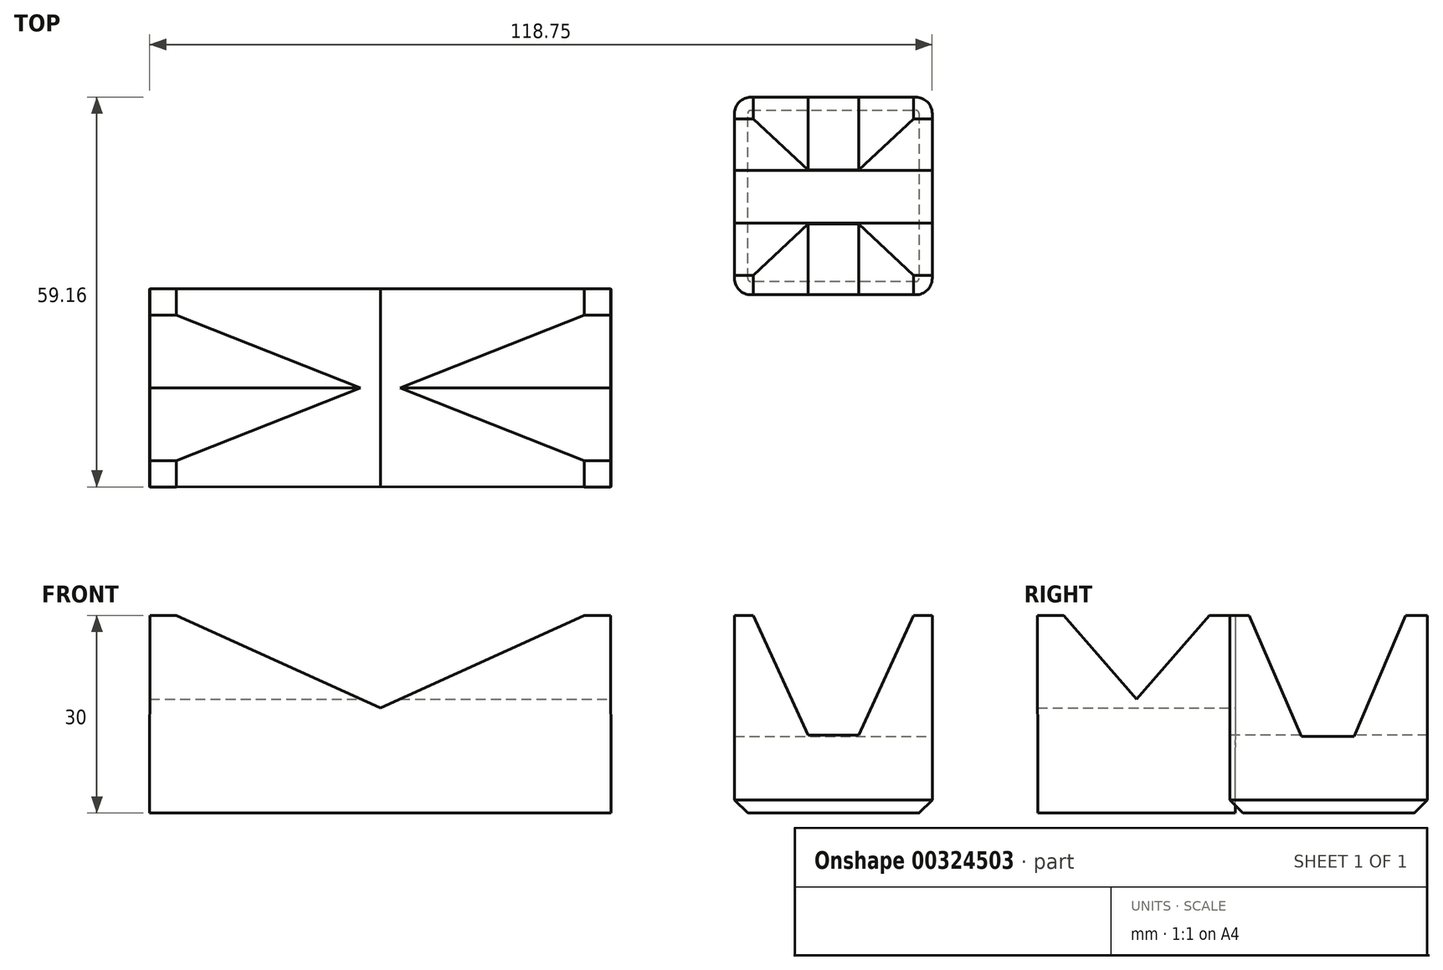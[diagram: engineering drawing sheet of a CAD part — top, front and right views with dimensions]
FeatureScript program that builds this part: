
annotation { "Feature Type Name" : "Feature", "Feature Type Description" : "" }
export const myFeature = defineFeature(function(context is Context, id is Id, definition is map)
    precondition{}
    {
        {
            var Q0;
            Q0=qCreatedBy(makeId("Top.planeOp"),FACE);
            var sketch = newSketch(context, id + "F0", { "sketchPlane" : qUnion([Q0])});
            skLineSegment(sketch, "E0.bottom", {"start": v(-35, 15) * mm, "end": v(35, 15) * mm});
            skLineSegment(sketch, "E0.top", {"start": v(-35, -15) * mm, "end": v(35, -15) * mm});
            skLineSegment(sketch, "E0.left", {"start": v(-35, 15) * mm, "end": v(-35, -15) * mm});
            skLineSegment(sketch, "E0.right", {"start": v(35, 15) * mm, "end": v(35, -15) * mm});
            skPoint(sketch, "E0.middle", {"position": v(0, 0) * mm});
            skSolve(sketch);
        }
        {
            var Q0;
            Q0=qCreatedBy(makeId("Top.planeOp"),FACE);
            cPlane(context, id + "F1", {"entities" : qUnion([Q0]), "cplaneType" : CPlaneType.OFFSET, "offset" : 30 * mm, "width" : 150 * mm, "height" : 150 * mm});
        }
        {
            var Q0;
            Q0=qCreatedBy(id+"F1.planeOp",FACE);
            var sketch = newSketch(context, id + "F2", { "sketchPlane" : qUnion([Q0])});
            skLineSegment(sketch, "E1", {"start": v(-34.94, 15.03) * mm, "end": v(-30.94, 15.03) * mm});
            skLineSegment(sketch, "E2", {"start": v(-30.94, 15.03) * mm, "end": v(-30.94, 11.03) * mm});
            skLineSegment(sketch, "E3", {"start": v(-30.94, 11.03) * mm, "end": v(-34.94, 11.03) * mm});
            skLineSegment(sketch, "E4", {"start": v(-34.94, 11.03) * mm, "end": v(-34.94, 15.03) * mm});
            skLineSegment(sketch, "E5.MirrorCS", {"start": v(-30.94, -15.03) * mm, "end": v(-30.94, -11.03) * mm});
            skLineSegment(sketch, "E6.MirrorCS", {"start": v(-34.94, -15.03) * mm, "end": v(-30.94, -15.03) * mm});
            skLineSegment(sketch, "E7.MirrorCS", {"start": v(-34.94, -11.03) * mm, "end": v(-34.94, -15.03) * mm});
            skLineSegment(sketch, "E8.MirrorCS", {"start": v(-30.94, -11.03) * mm, "end": v(-34.94, -11.03) * mm});
            skLineSegment(sketch, "E9.MirrorCS", {"start": v(30.94, 15.03) * mm, "end": v(30.94, 11.03) * mm});
            skLineSegment(sketch, "E10.MirrorCS", {"start": v(34.94, 15.03) * mm, "end": v(30.94, 15.03) * mm});
            skLineSegment(sketch, "E11.MirrorCS", {"start": v(34.94, 11.03) * mm, "end": v(34.94, 15.03) * mm});
            skLineSegment(sketch, "E12.MirrorCS", {"start": v(30.94, 11.03) * mm, "end": v(34.94, 11.03) * mm});
            skLineSegment(sketch, "E13.MirrorCS", {"start": v(30.94, -11.03) * mm, "end": v(34.94, -11.03) * mm});
            skLineSegment(sketch, "E14.MirrorCS", {"start": v(30.94, -15.03) * mm, "end": v(30.94, -11.03) * mm});
            skLineSegment(sketch, "E15.MirrorCS", {"start": v(34.94, -15.03) * mm, "end": v(30.94, -15.03) * mm});
            skLineSegment(sketch, "E16.MirrorCS", {"start": v(34.94, -11.03) * mm, "end": v(34.94, -15.03) * mm});
            skSolve(sketch);
        }
        {
            var Q0;
            Q0=makeQuery(id+"F0.imprint","IMPRINT",FACE,{"disambiguationData":[TD([[makeQuery(id+"F0.imprint","IMPRINT",EDGE,{"derivedFrom":sQuery(id+"F0.wireOp",EDGE,"E0.bottom")}),-1.0]])]});
            var Q1;
            Q1=makeQuery(id+"F2.imprint","IMPRINT",FACE,{"disambiguationData":[TD([[makeQuery(id+"F2.imprint","IMPRINT",EDGE,{"derivedFrom":sQuery(id+"F2.wireOp",EDGE,"E1")}),-1.0]])]});
            loft(context, id + "F3", {"sheetProfilesArray" : [{ "sheetProfileEntities" : qUnion([Q0]) }, { "sheetProfileEntities" : qUnion([Q1]) }]});
        }
        {
            var Q1;
            Q1 = qSketchRegion(id + "F0", true);
            var Q2;
            Q2=makeQuery(id+"F2.imprint","IMPRINT",FACE,{"disambiguationData":[TD([[makeQuery(id+"F2.imprint","IMPRINT",EDGE,{"derivedFrom":sQuery(id+"F2.wireOp",EDGE,"E5.MirrorCS")}),1.0]])]});
            loft(context, id + "F4", {"operationType" : NewBodyOperationType.ADD, "sheetProfilesArray" : [{ "sheetProfileEntities" : qUnion([Q1]) }, { "sheetProfileEntities" : qUnion([Q2]) }]});
        }
        {
            var Q1;
            Q1 = qSketchRegion(id + "F0", true);
            var Q2;
            Q2=makeQuery(id+"F2.imprint","IMPRINT",FACE,{"disambiguationData":[TD([[makeQuery(id+"F2.imprint","IMPRINT",EDGE,{"derivedFrom":sQuery(id+"F2.wireOp",EDGE,"E9.MirrorCS")}),1.0]])]});
            loft(context, id + "F5", {"operationType" : NewBodyOperationType.ADD, "sheetProfilesArray" : [{ "sheetProfileEntities" : qUnion([Q1]) }, { "sheetProfileEntities" : qUnion([Q2]) }]});
        }
        {
            var Q1;
            Q1 = qSketchRegion(id + "F0", true);
            var Q2;
            Q2=makeQuery(id+"F2.imprint","IMPRINT",FACE,{"disambiguationData":[TD([[makeQuery(id+"F2.imprint","IMPRINT",EDGE,{"derivedFrom":sQuery(id+"F2.wireOp",EDGE,"E13.MirrorCS")}),-1.0]])]});
            loft(context, id + "F6", {"operationType" : NewBodyOperationType.ADD, "sheetProfilesArray" : [{ "sheetProfileEntities" : qUnion([Q1]) }, { "sheetProfileEntities" : qUnion([Q2]) }]});
        }
        {
            var Q0;
            Q0=qCreatedBy(makeId("Top.planeOp"),FACE);
            var sketch = newSketch(context, id + "F7", { "sketchPlane" : qUnion([Q0])});
            skLineSegment(sketch, "E17", {"start": v(83.75, 44.13) * mm, "end": v(53.75, 44.13) * mm});
            skLineSegment(sketch, "E18", {"start": v(53.75, 44.13) * mm, "end": v(53.75, 14.13) * mm});
            skLineSegment(sketch, "E19", {"start": v(53.75, 14.13) * mm, "end": v(83.75, 14.13) * mm});
            skLineSegment(sketch, "E20", {"start": v(83.75, 14.13) * mm, "end": v(83.75, 44.13) * mm});
            skSolve(sketch);
        }
        {
            var Q0;
            Q0=makeQuery(id+"F7.imprint","IMPRINT",FACE,{"disambiguationData":[TD([[makeQuery(id+"F7.imprint","IMPRINT",EDGE,{"derivedFrom":sQuery(id+"F7.wireOp",EDGE,"E17")}),1.0]])]});
            extrude(context, id + "F8", {"entities" : qUnion([Q0]), "depth" : 30 * mm});
        }
        {
            var Q0;
            Q0=makeQuery(id+"F8.opExtrude","SWEPT_FACE",FACE,{"disambiguationData":[OSD([sQuery(id+"F7.wireOp",EDGE,"E19")])]});
            var sketch = newSketch(context, id + "F9", { "sketchPlane" : qUnion([Q0])});
            skLineSegment(sketch, "E21", {"start": v(56.6, 30) * mm, "end": v(64.93, 11.82) * mm});
            skLineSegment(sketch, "E22", {"start": v(64.93, 11.82) * mm, "end": v(68.75, 11.82) * mm});
            skLineSegment(sketch, "E23.MirrorCS", {"start": v(80.91, 30) * mm, "end": v(72.58, 11.82) * mm});
            skLineSegment(sketch, "E24.MirrorCS", {"start": v(72.58, 11.82) * mm, "end": v(68.75, 11.82) * mm});
            skSolve(sketch);
        }
        {
            var Q0;
            {var subQ1=sQuery(id+"F9.wireOp",EDGE,"E21");Q0=makeQuery(id+"F9.imprint","IMPRINT",FACE,{"disambiguationData":[TD([[makeQuery(id+"F9.imprint","IMPRINT",EDGE,{"derivedFrom":subQ1}),1.0]])]});}
            extrude(context, id + "F10", {"entities" : qUnion([Q0]), "operationType" : NewBodyOperationType.REMOVE, "oppositeDirection" : true, "depth" : 30 * mm});
        }
        {
            var Q0;
            Q0=makeQuery(id+"F8.opExtrude","SWEPT_FACE",FACE,{"disambiguationData":[OSD([sQuery(id+"F7.wireOp",EDGE,"E20")])]});
            var sketch = newSketch(context, id + "F11", { "sketchPlane" : qUnion([Q0])});
            skLineSegment(sketch, "E25", {"start": v(17.09, 30) * mm, "end": v(24.99, 11.63) * mm});
            skLineSegment(sketch, "E26", {"start": v(24.99, 11.63) * mm, "end": v(32.99, 11.63) * mm});
            skLineSegment(sketch, "E27", {"start": v(32.99, 11.63) * mm, "end": v(40.82, 30) * mm});
            skSolve(sketch);
        }
        {
            var Q0;
            {var subQ0=sQuery(id+"F11.wireOp",EDGE,"E25");Q0=makeQuery(id+"F11.imprint","IMPRINT",FACE,{"disambiguationData":[TD([[makeQuery(id+"F11.imprint","IMPRINT",EDGE,{"derivedFrom":subQ0}),1.0]])]});}
            extrude(context, id + "F12", {"entities" : qUnion([Q0]), "operationType" : NewBodyOperationType.REMOVE, "oppositeDirection" : true, "depth" : 30 * mm});
        }
        {
            var Q0;
            Q0=makeQuery(id+"F8.opExtrude","SWEPT_EDGE",EDGE,{"disambiguationData":[OSD([sQuery(id+"F7.wireOp",EDGE,"E19"),sQuery(id+"F7.wireOp",EDGE,"E20")])]});
            var Q1;
            Q1=makeQuery(id+"F8.opExtrude","SWEPT_EDGE",EDGE,{"disambiguationData":[OSD([sQuery(id+"F7.wireOp",EDGE,"E18"),sQuery(id+"F7.wireOp",EDGE,"E19")])]});
            var Q2;
            Q2=makeQuery(id+"F8.opExtrude","SWEPT_EDGE",EDGE,{"disambiguationData":[OSD([sQuery(id+"F7.wireOp",EDGE,"E17"),sQuery(id+"F7.wireOp",EDGE,"E20")])]});
            var Q3;
            Q3=makeQuery(id+"F8.opExtrude","SWEPT_EDGE",EDGE,{"disambiguationData":[OSD([sQuery(id+"F7.wireOp",EDGE,"E17"),sQuery(id+"F7.wireOp",EDGE,"E18")])]});
            fillet(context, id + "F13", {"entities" : qUnion([Q0, Q1, Q2, Q3]), "radius" : 2.5 * mm, "tangentPropagation" : true, "allowEdgeOverflow" : false});
        }
        {
            var Q0;
            Q0=makeQuery(id+"F8.opExtrude","CAP_EDGE",EDGE,{"disambiguationData":[OSD([sQuery(id+"F7.wireOp",EDGE,"E20")])],"isStart":true});
            chamfer(context, id + "F14", {"entities" : qUnion([Q0]), "width" : 2 * mm, "tangentPropagation" : true});
        }
        {
            var Q0;
            Q0=makeQuery(id+"F0.imprint","IMPRINT",FACE,{"disambiguationData":[TD([[makeQuery(id+"F0.imprint","IMPRINT",EDGE,{"derivedFrom":sQuery(id+"F0.wireOp",EDGE,"E0.bottom")}),-1.0]])]});
            var sketch = newSketch(context, id + "F15", { "sketchPlane" : qUnion([Q0])});
            skFitSpline(sketch, "E28", {"points": [v(34.97, 15.08) * mm, v(32.63, 12.63) * mm, v(28.6, 12.18) * mm, v(27.82, 9.83) * mm, v(29.6, 8.38) * mm, v(30.17, 6.26) * mm, v(28.5, 4.13) * mm, v(27.93, 1.68) * mm, v(29.39, -0.67) * mm, v(28.71, -2.68) * mm, v(27.37, -6.7) * mm, v(28.27, -9.72) * mm, v(31.84, -12.63) * mm, v(35.08, -15.2) * mm, v(35.1, -15.12) * mm], "startDerivative": vector(-23.22, -40.02) * mm, "endDerivative": vector(-0.4, 8.86) * mm});
            skLineSegment(sketch, "E29", {"start": v(0, 0) * mm, "end": v(0, 16.7) * mm});
            skFitSpline(sketch, "E30.MirrorCS", {"points": [v(-34.97, 15.08) * mm, v(-32.63, 12.63) * mm, v(-28.6, 12.18) * mm, v(-27.82, 9.83) * mm, v(-29.6, 8.38) * mm, v(-30.17, 6.26) * mm, v(-28.5, 4.13) * mm, v(-27.93, 1.68) * mm, v(-29.39, -0.67) * mm, v(-28.71, -2.68) * mm, v(-27.37, -6.7) * mm, v(-28.27, -9.72) * mm, v(-31.84, -12.63) * mm, v(-35.08, -15.2) * mm, v(-35.1, -15.12) * mm], "startDerivative": vector(23.22, -40.02) * mm, "endDerivative": vector(0.4, 8.86) * mm});
            skFitSpline(sketch, "E31", {"points": [v(30.8, 15.12) * mm, v(23.6, 13.53) * mm, v(22.6, 10.77) * mm, v(24.69, 8.5) * mm, v(25.86, 6.75) * mm, v(24.77, 4.15) * mm, v(23.77, 2.06) * mm, v(24.02, 0) * mm, v(23.68, -3.38) * mm, v(23.01, -5.8) * mm, v(23.43, -9.07) * mm, v(26.61, -13.84) * mm, v(30.8, -14.93) * mm], "startDerivative": vector(-69.61, -5.08) * mm, "endDerivative": vector(46.55, -3.2) * mm});
            skFitSpline(sketch, "E32.MirrorCS", {"points": [v(-30.8, 15.12) * mm, v(-23.6, 13.53) * mm, v(-22.6, 10.77) * mm, v(-24.69, 8.5) * mm, v(-25.86, 6.75) * mm, v(-24.77, 4.15) * mm, v(-23.77, 2.06) * mm, v(-24.02, 0) * mm, v(-23.68, -3.38) * mm, v(-23.01, -5.8) * mm, v(-23.43, -9.07) * mm, v(-26.61, -13.84) * mm, v(-30.8, -14.93) * mm], "startDerivative": vector(69.61, -5.08) * mm, "endDerivative": vector(-46.55, -3.2) * mm});
            skLineSegment(sketch, "E33", {"start": v(30.8, 15.12) * mm, "end": v(34.97, 15.08) * mm});
            skLineSegment(sketch, "E34", {"start": v(-30.8, 15.12) * mm, "end": v(-34.97, 15.08) * mm});
            skLineSegment(sketch, "E35", {"start": v(34.97, 15.08) * mm, "end": v(30.8, 15.12) * mm});
            skLineSegment(sketch, "E36", {"start": v(35.1, -15.15) * mm, "end": v(30.8, -14.93) * mm});
            skLineSegment(sketch, "E37", {"start": v(-30.8, -14.93) * mm, "end": v(-35.08, -15.2) * mm});
            skSolve(sketch);
        }
        {
            var Q0;
            Q0 = qSketchRegion(id + "F15", true);
            extrude(context, id + "F16", {"entities" : qUnion([Q0]), "operationType" : NewBodyOperationType.REMOVE, "oppositeDirection" : true, "depth" : 1 * mm});
        }
        {
            var Q0;
            Q0=sQuery(id+"F15.wireOp",EDGE,"E32.MirrorCS");
            var Q1;
            Q1=sQuery(id+"F15.wireOp",EDGE,"E30.MirrorCS");
            var Q2;
            Q2=sQuery(id+"F15.wireOp",EDGE,"E31");
            var Q3;
            Q3=sQuery(id+"F15.wireOp",EDGE,"E28");
            extrude(context, id + "F17", {"bodyType" : ToolBodyType.SURFACE, "surfaceEntities" : qUnion([Q0, Q1, Q2, Q3]), "depth" : 1 * mm});
        }
    });
